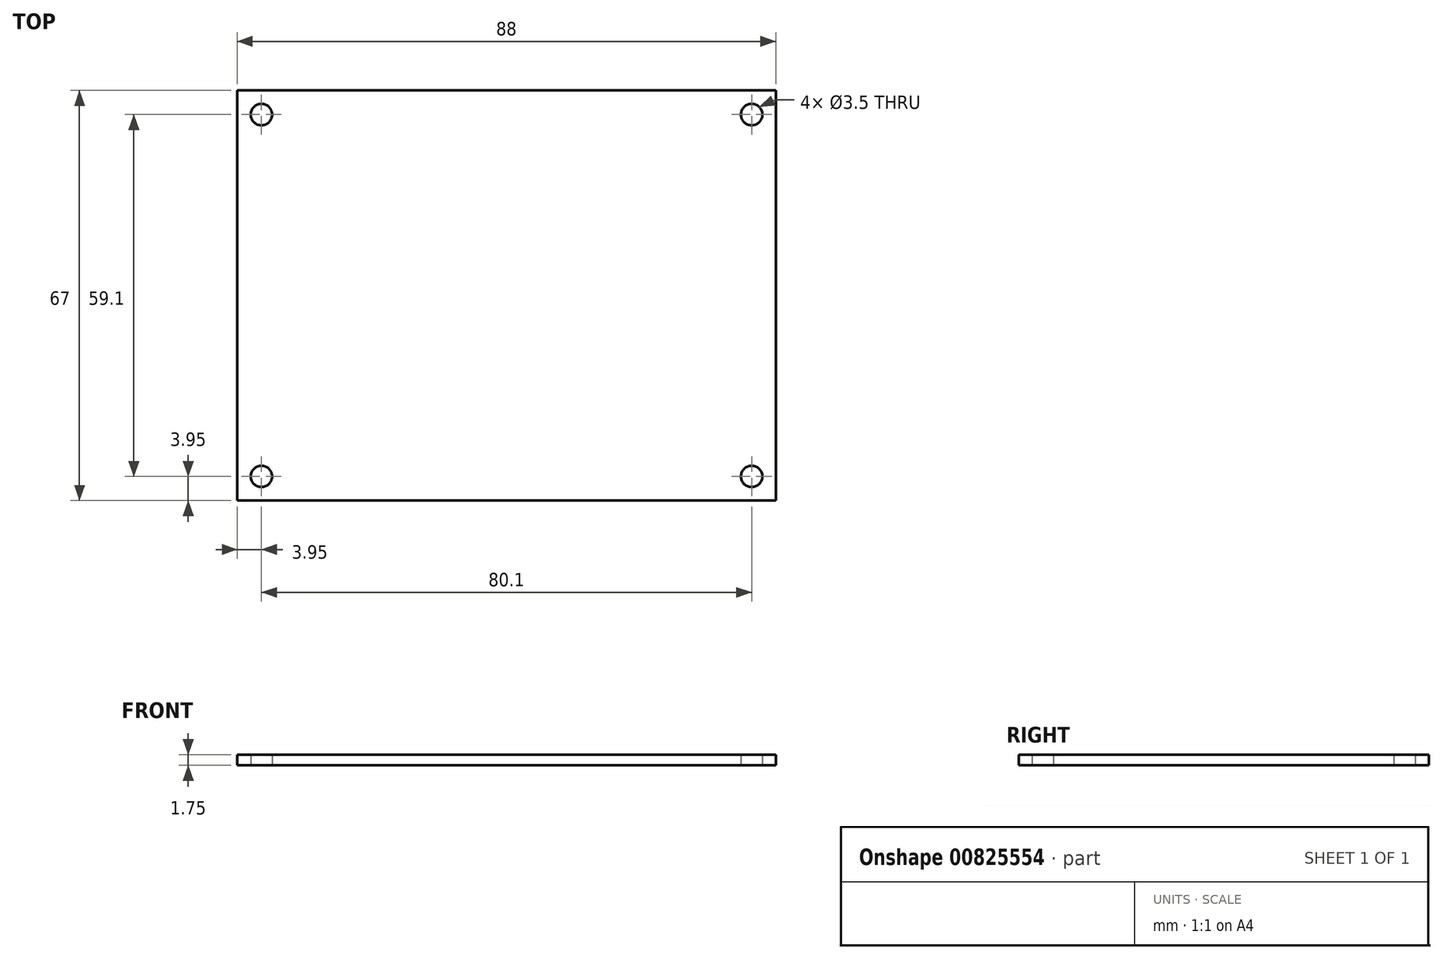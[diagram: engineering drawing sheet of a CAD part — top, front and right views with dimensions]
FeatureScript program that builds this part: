
annotation { "Feature Type Name" : "Feature", "Feature Type Description" : "" }
export const myFeature = defineFeature(function(context is Context, id is Id, definition is map)
    precondition{}
    {
        {
            var Q0;
            Q0=qCreatedBy(makeId("Top.planeOp"),FACE);
            var sketch = newSketch(context, id + "F0", { "sketchPlane" : qUnion([Q0])});
            skLineSegment(sketch, "E0.bottom", {"start": v(44, -33.5) * mm, "end": v(-44, -33.5) * mm});
            skLineSegment(sketch, "E0.top", {"start": v(44, 33.5) * mm, "end": v(-44, 33.5) * mm});
            skLineSegment(sketch, "E0.left", {"start": v(44, -33.5) * mm, "end": v(44, 33.5) * mm});
            skLineSegment(sketch, "E0.right", {"start": v(-44, -33.5) * mm, "end": v(-44, 33.5) * mm});
            skPoint(sketch, "E0.middle", {"position": v(0, 0) * mm});
            skCircle(sketch, "E1", {"center": v(40.05, 29.55) * mm, "radius": 1.75 * mm});
            skCircle(sketch, "E2.MirrorC", {"center": v(-40.05, 29.55) * mm, "radius": 1.75 * mm});
            skCircle(sketch, "E3.MirrorC", {"center": v(-40.05, -29.55) * mm, "radius": 1.75 * mm});
            skCircle(sketch, "E4.MirrorC", {"center": v(40.05, -29.55) * mm, "radius": 1.75 * mm});
            skSolve(sketch);
        }
        {
            var Q0;
            Q0=makeQuery(id+"F0.imprint","IMPRINT",FACE,{"disambiguationData":[TD([[makeQuery(id+"F0.imprint","IMPRINT",EDGE,{"derivedFrom":sQuery(id+"F0.wireOp",EDGE,"E0.bottom")}),-1.0]])]});
            extrude(context, id + "F1", {"entities" : qUnion([Q0]), "depth" : 1.75 * mm, "offsetDistance" : 25 * mm});
        }
    });
